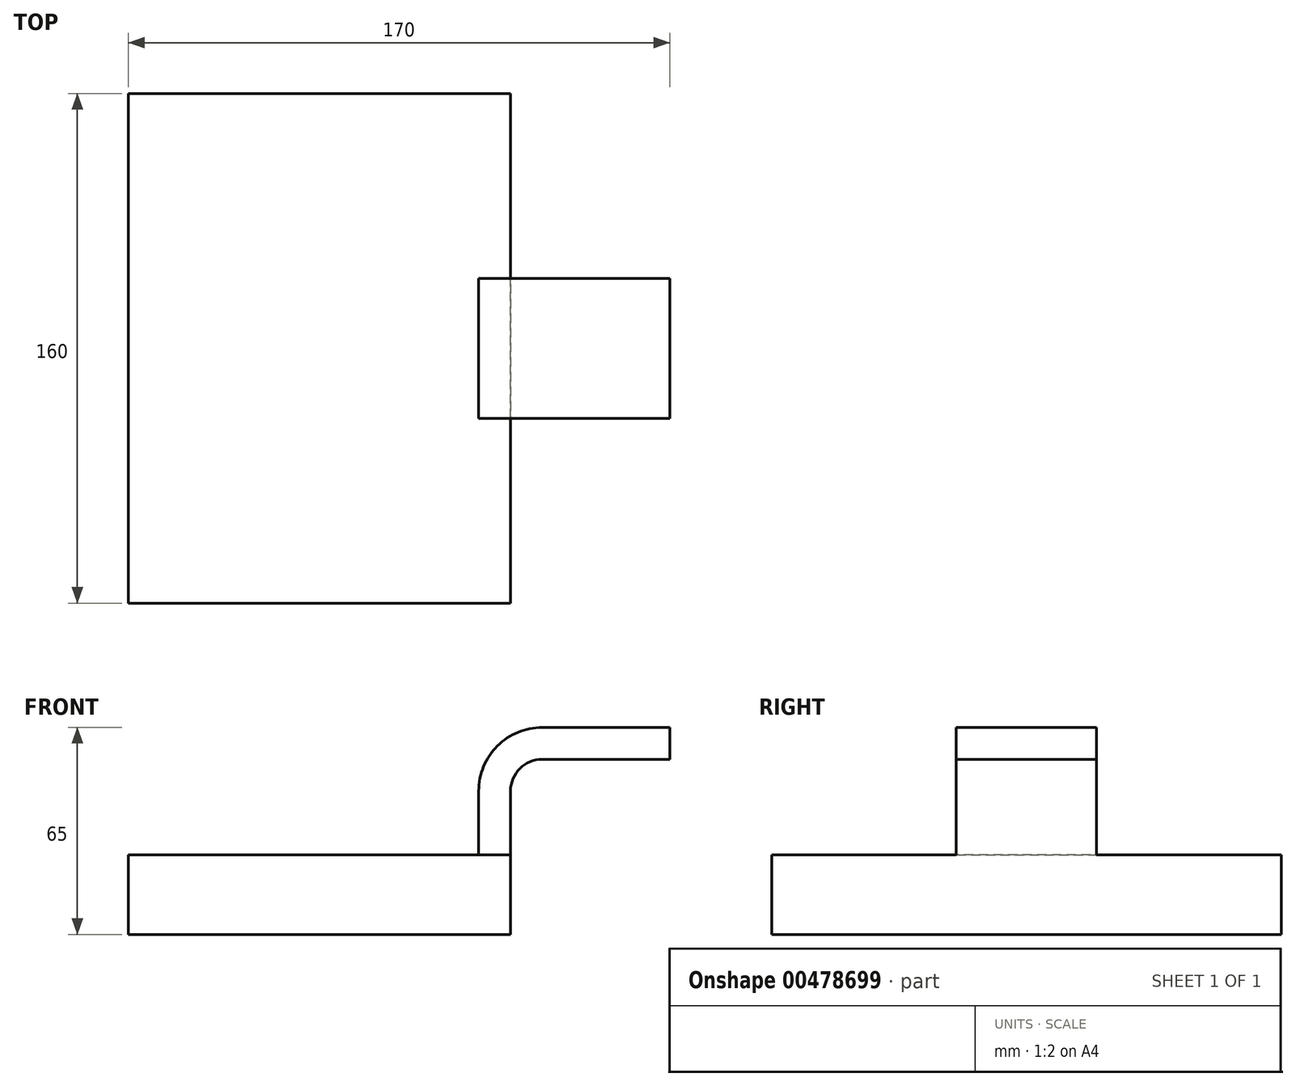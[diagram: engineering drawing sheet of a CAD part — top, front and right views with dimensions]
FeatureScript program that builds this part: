
annotation { "Feature Type Name" : "Feature", "Feature Type Description" : "" }
export const myFeature = defineFeature(function(context is Context, id is Id, definition is map)
    precondition{}
    {
        {
            var Q0;
            Q0=qCreatedBy(makeId("Front.planeOp"),FACE);
            var sketch = newSketch(context, id + "F0", { "sketchPlane" : qUnion([Q0])});
            skLineSegment(sketch, "E0.bottom", {"start": v(60, 12.5) * mm, "end": v(-60, 12.5) * mm});
            skLineSegment(sketch, "E0.top", {"start": v(60, -12.5) * mm, "end": v(-60, -12.5) * mm});
            skLineSegment(sketch, "E0.left", {"start": v(60, 12.5) * mm, "end": v(60, -12.5) * mm});
            skLineSegment(sketch, "E0.right", {"start": v(-60, 12.5) * mm, "end": v(-60, -12.5) * mm});
            skPoint(sketch, "E0.middle", {"position": v(0, 0) * mm});
            skLineSegment(sketch, "E1.bottom", {"start": v(80, 57.5) * mm, "end": v(140, 57.5) * mm});
            skLineSegment(sketch, "E1.top", {"start": v(80, 27.5) * mm, "end": v(140, 27.5) * mm});
            skLineSegment(sketch, "E1.left", {"start": v(80, 57.5) * mm, "end": v(80, 27.5) * mm});
            skLineSegment(sketch, "E1.right", {"start": v(140, 57.5) * mm, "end": v(140, 27.5) * mm});
            skPoint(sketch, "E1.middle", {"position": v(110, 42.5) * mm});
            skLineSegment(sketch, "E2", {"start": v(60, 12.5) * mm, "end": v(60, 32.5) * mm});
            skLineSegment(sketch, "E3", {"start": v(70, 42.5) * mm, "end": v(110, 42.5) * mm});
            skArc(sketch, "E4", {"start": v(60, 32.5) * mm, "mid": v(62.93, 39.57) * mm, "end": v(70, 42.5) * mm});
            skLineSegment(sketch, "E5.0", {"start": v(70, 52.5) * mm, "end": v(110, 52.5) * mm});
            skArc(sketch, "E5.1", {"start": v(50, 32.5) * mm, "mid": v(55.86, 46.64) * mm, "end": v(70, 52.5) * mm});
            skLineSegment(sketch, "E5.2", {"start": v(50, 12.5) * mm, "end": v(50, 32.5) * mm});
            skLineSegment(sketch, "E6", {"start": v(110, 27.5) * mm, "end": v(110, 57.5) * mm});
            skFitSpline(sketch, "E7", {"points": [v(-60, 12.5) * mm, v(70, 52.5) * mm], "startDerivative": vector(0, 122.9) * mm, "endDerivative": vector(210, 0) * mm});
            skSolve(sketch);
        }
        {
            var Q0;
            Q0=makeQuery(id+"F0.imprint","IMPRINT",FACE,{"disambiguationData":[TD([[makeQuery(id+"F0.imprint","IMPRINT",EDGE,{"derivedFrom":sQuery(id+"F0.wireOp",EDGE,"E0.top")}),-1.0]])]});
            extrude(context, id + "F1", {"entities" : qUnion([Q0]), "endBound" : BoundingType.SYMMETRIC, "oppositeDirection" : true, "depth" : 160 * mm});
        }
        {
            var Q0;
            {var subQ4=sQuery(id+"F0.wireOp",EDGE,"E2");Q0=makeQuery(id+"F0.imprint","IMPRINT",FACE,{"disambiguationData":[TD([[makeQuery(id+"F0.imprint","IMPRINT",EDGE,{"derivedFrom":subQ4}),1.0]])]});}
            var Q1;
            {var subQ0=sQuery(id+"F0.wireOp",EDGE,"E5.0");var subQ1=sQuery(id+"F0.wireOp",EDGE,"E1.left");var subQ2=makeQuery(id+"F0.imprint","INTERSECT",VERTEX,{"derivedFrom":[subQ1,subQ0]});Q1=makeQuery(id+"F0.imprint","IMPRINT",FACE,{"disambiguationData":[TD([[makeQuery(id+"F0.imprint","IMPRINT",EDGE,{"disambiguationData":[TD([[subQ2,-1.0]])],"derivedFrom":subQ1}),1.0]])]});}
            extrude(context, id + "F2", {"entities" : qUnion([Q0, Q1]), "operationType" : NewBodyOperationType.ADD, "endBound" : BoundingType.SYMMETRIC, "depth" : 44 * mm});
        }
        {
            var Q0;
            Q0=makeQuery(id+"F0.imprint","IMPRINT",FACE,{"disambiguationData":[TD([[makeQuery(id+"F0.imprint","IMPRINT",EDGE,{"derivedFrom":sQuery(id+"F0.wireOp",EDGE,"E5.1")}),1.0]])]});
            extrude(context, id + "F3", {"entities" : qUnion([Q0]), "operationType" : NewBodyOperationType.ADD, "endBound" : BoundingType.SYMMETRIC, "depth" : 25.8 * mm});
        }
    });
